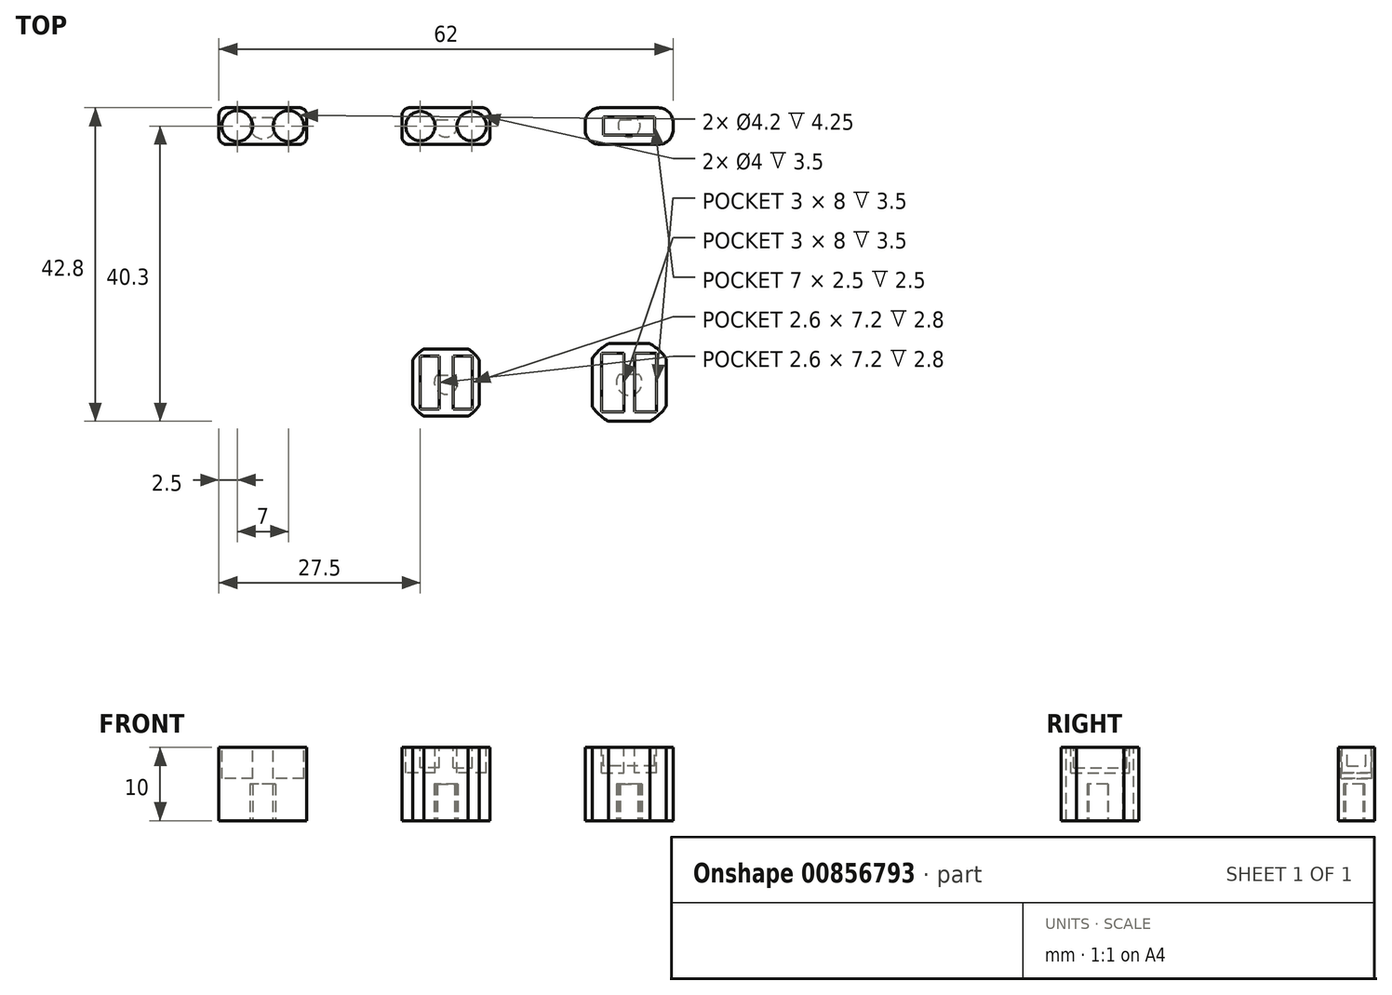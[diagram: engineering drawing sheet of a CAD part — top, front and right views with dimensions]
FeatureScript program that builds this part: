
annotation { "Feature Type Name" : "Feature", "Feature Type Description" : "" }
export const myFeature = defineFeature(function(context is Context, id is Id, definition is map)
    precondition{}
    {
        {
            var Q0;
            Q0=qCreatedBy(makeId("Top.planeOp"),FACE);
            var sketch = newSketch(context, id + "F0", { "sketchPlane" : qUnion([Q0])});
            skCircle(sketch, "E0", {"center": v(0, -10) * mm, "radius": 7 * mm});
            skLineSegment(sketch, "E1.bottom", {"start": v(6, -12.5) * mm, "end": v(-6, -12.5) * mm});
            skLineSegment(sketch, "E1.top", {"start": v(6, -7.5) * mm, "end": v(-6, -7.5) * mm});
            skLineSegment(sketch, "E1.left", {"start": v(6, -12.5) * mm, "end": v(6, -7.5) * mm});
            skLineSegment(sketch, "E1.right", {"start": v(-6, -12.5) * mm, "end": v(-6, -7.5) * mm});
            skCircle(sketch, "E2", {"center": v(-3.5, -10) * mm, "radius": 2 * mm});
            skCircle(sketch, "E3", {"center": v(3.5, -10) * mm, "radius": 2 * mm});
            skLineSegment(sketch, "E4", {"start": v(12.5, 0) * mm, "end": v(12.5, -20) * mm, "construction": true});
            skLineSegment(sketch, "E5.MirrorCS", {"start": v(31, -12.5) * mm, "end": v(31, -7.5) * mm});
            skLineSegment(sketch, "E6.MirrorCS", {"start": v(19, -7.5) * mm, "end": v(31, -7.5) * mm});
            skLineSegment(sketch, "E7.MirrorCS", {"start": v(19, -12.5) * mm, "end": v(31, -12.5) * mm});
            skLineSegment(sketch, "E8.MirrorCS", {"start": v(19, -12.5) * mm, "end": v(19, -7.5) * mm});
            skCircle(sketch, "E9.MirrorC", {"center": v(25, -10) * mm, "radius": 7 * mm});
            skLineSegment(sketch, "E10.bottom", {"start": v(28.5, -11.25) * mm, "end": v(21.5, -11.25) * mm});
            skLineSegment(sketch, "E10.top", {"start": v(28.5, -8.75) * mm, "end": v(21.5, -8.75) * mm});
            skLineSegment(sketch, "E10.left", {"start": v(28.5, -11.25) * mm, "end": v(28.5, -8.75) * mm});
            skLineSegment(sketch, "E10.right", {"start": v(21.5, -11.25) * mm, "end": v(21.5, -8.75) * mm});
            skCircle(sketch, "E11", {"center": v(0, -45) * mm, "radius": 7 * mm});
            skLineSegment(sketch, "E12.bottom", {"start": v(-0.95, -48.6) * mm, "end": v(-3.55, -48.6) * mm});
            skLineSegment(sketch, "E12.top", {"start": v(-0.95, -41.4) * mm, "end": v(-3.55, -41.4) * mm});
            skLineSegment(sketch, "E12.left", {"start": v(-0.95, -48.6) * mm, "end": v(-0.95, -41.4) * mm});
            skLineSegment(sketch, "E12.right", {"start": v(-3.55, -48.6) * mm, "end": v(-3.55, -41.4) * mm});
            skPoint(sketch, "E12.middle", {"position": v(-2.25, -45) * mm});
            skLineSegment(sketch, "E13", {"start": v(0, -45) * mm, "end": v(9.52, -45) * mm, "construction": true});
            skLineSegment(sketch, "E14.MirrorCS", {"start": v(0.95, -48.6) * mm, "end": v(0.95, -41.4) * mm});
            skLineSegment(sketch, "E15.MirrorCS", {"start": v(0.95, -41.4) * mm, "end": v(3.55, -41.4) * mm});
            skLineSegment(sketch, "E16.MirrorCS", {"start": v(0.95, -48.6) * mm, "end": v(3.55, -48.6) * mm});
            skLineSegment(sketch, "E17.MirrorCS", {"start": v(3.55, -48.6) * mm, "end": v(3.55, -41.4) * mm});
            skPoint(sketch, "E18.MirrorP", {"position": v(2.25, -45) * mm});
            skCircle(sketch, "E19", {"center": v(0, -45) * mm, "radius": 5.5 * mm});
            skLineSegment(sketch, "E20", {"start": v(-3.01, -40.4) * mm, "end": v(3.01, -40.4) * mm});
            skLineSegment(sketch, "E21", {"start": v(-4.55, -41.91) * mm, "end": v(-4.55, -48.09) * mm});
            skLineSegment(sketch, "E22.MirrorCS", {"start": v(4.55, -41.91) * mm, "end": v(4.55, -48.09) * mm});
            skLineSegment(sketch, "E23.MirrorCS", {"start": v(-3.01, -49.6) * mm, "end": v(3.01, -49.6) * mm});
            skCircle(sketch, "E24", {"center": v(25, -45) * mm, "radius": 6 * mm});
            skCircle(sketch, "E25", {"center": v(25, -45) * mm, "radius": 7 * mm});
            skLineSegment(sketch, "E26.bottom", {"start": v(28.75, -49) * mm, "end": v(25.75, -49) * mm});
            skLineSegment(sketch, "E26.top", {"start": v(28.75, -41) * mm, "end": v(25.75, -41) * mm});
            skLineSegment(sketch, "E26.left", {"start": v(28.75, -49) * mm, "end": v(28.75, -41) * mm});
            skLineSegment(sketch, "E26.right", {"start": v(25.75, -49) * mm, "end": v(25.75, -41) * mm});
            skPoint(sketch, "E26.middle", {"position": v(27.25, -45) * mm});
            skLineSegment(sketch, "E27", {"start": v(25, -45) * mm, "end": v(25, -28.58) * mm, "construction": true});
            skLineSegment(sketch, "E28.MirrorCS", {"start": v(21.25, -41) * mm, "end": v(24.25, -41) * mm});
            skLineSegment(sketch, "E29.MirrorCS", {"start": v(21.25, -49) * mm, "end": v(21.25, -41) * mm});
            skLineSegment(sketch, "E30.MirrorCS", {"start": v(24.25, -49) * mm, "end": v(24.25, -41) * mm});
            skLineSegment(sketch, "E31.MirrorCS", {"start": v(21.25, -49) * mm, "end": v(24.25, -49) * mm});
            skLineSegment(sketch, "E32", {"start": v(27.81, -50.3) * mm, "end": v(22.19, -50.3) * mm});
            skLineSegment(sketch, "E33", {"start": v(19.95, -48.24) * mm, "end": v(19.95, -41.76) * mm});
            skLineSegment(sketch, "E34", {"start": v(22.19, -39.7) * mm, "end": v(27.81, -39.7) * mm});
            skLineSegment(sketch, "E35", {"start": v(30.05, -41.76) * mm, "end": v(30.05, -48.24) * mm});
            skLineSegment(sketch, "E36", {"start": v(-12.5, -20.28) * mm, "end": v(-12.5, 0) * mm, "construction": true});
            skCircle(sketch, "E37.MirrorC", {"center": v(-25, -10) * mm, "radius": 7 * mm});
            skLineSegment(sketch, "E38.MirrorCS", {"start": v(-31, -12.5) * mm, "end": v(-19, -12.5) * mm});
            skLineSegment(sketch, "E39.MirrorCS", {"start": v(-19, -12.5) * mm, "end": v(-19, -7.5) * mm});
            skLineSegment(sketch, "E40.MirrorCS", {"start": v(-31, -7.5) * mm, "end": v(-19, -7.5) * mm});
            skLineSegment(sketch, "E41.MirrorCS", {"start": v(-31, -12.5) * mm, "end": v(-31, -7.5) * mm});
            skCircle(sketch, "E42", {"center": v(-28.5, -10) * mm, "radius": 2.1 * mm});
            skCircle(sketch, "E43", {"center": v(-21.5, -10) * mm, "radius": 2.1 * mm});
            skSolve(sketch);
        }
        {
            var Q0;
            Q0=makeQuery(id+"F0.imprint","IMPRINT",FACE,{"disambiguationData":[TD([[makeQuery(id+"F0.imprint","IMPRINT",EDGE,{"derivedFrom":sQuery(id+"F0.wireOp",EDGE,"E1.bottom")}),-1.0]])]});
            var Q1;
            Q1=makeQuery(id+"F0.imprint","IMPRINT",FACE,{"disambiguationData":[TD([[makeQuery(id+"F0.imprint","IMPRINT",EDGE,{"derivedFrom":sQuery(id+"F0.wireOp",EDGE,"E2")}),1.0]])]});
            var Q2;
            Q2=makeQuery(id+"F0.imprint","IMPRINT",FACE,{"disambiguationData":[TD([[makeQuery(id+"F0.imprint","IMPRINT",EDGE,{"derivedFrom":sQuery(id+"F0.wireOp",EDGE,"E3")}),1.0]])]});
            extrude(context, id + "F1", {"entities" : qUnion([Q0, Q1, Q2]), "oppositeDirection" : true, "depth" : 10 * mm, "offsetDistance" : 25 * mm});
        }
        {
            var Q0;
            Q0=makeQuery(id+"F0.imprint","IMPRINT",FACE,{"disambiguationData":[TD([[makeQuery(id+"F0.imprint","IMPRINT",EDGE,{"derivedFrom":sQuery(id+"F0.wireOp",EDGE,"E2")}),1.0]])]});
            var Q1;
            Q1=makeQuery(id+"F0.imprint","IMPRINT",FACE,{"disambiguationData":[TD([[makeQuery(id+"F0.imprint","IMPRINT",EDGE,{"derivedFrom":sQuery(id+"F0.wireOp",EDGE,"E3")}),1.0]])]});
            extrude(context, id + "F2", {"entities" : qUnion([Q0, Q1]), "operationType" : NewBodyOperationType.REMOVE, "oppositeDirection" : true, "depth" : 3.5 * mm, "offsetDistance" : 25 * mm});
        }
        {
            var Q0;
            Q0=makeQuery(id+"F1.opExtrude","CAP_FACE",FACE,{"disambiguationData":[OSD([sQuery(id+"F0.wireOp",EDGE,"E1.bottom"),sQuery(id+"F0.wireOp",EDGE,"E1.top"),sQuery(id+"F0.wireOp",EDGE,"E1.left"),sQuery(id+"F0.wireOp",EDGE,"E1.right")])],"isStart":false});
            var sketch = newSketch(context, id + "F3", { "sketchPlane" : qUnion([Q0])});
            skCircle(sketch, "E44", {"center": v(0, 10) * mm, "radius": 1.5 * mm});
            skPoint(sketch, "E44.centerSnap0", {"position": v(6, 10) * mm});
            skCircle(sketch, "E45", {"center": v(0, 10) * mm, "radius": 2.5 * mm});
            skLineSegment(sketch, "E46", {"start": v(-1.2, 9.1) * mm, "end": v(1.2, 9.1) * mm});
            skSolve(sketch);
        }
        {
            var Q0;
            Q0=makeQuery(id+"F1.opExtrude","SWEPT_EDGE",EDGE,{"disambiguationData":[OSD([sQuery(id+"F0.wireOp",EDGE,"E1.bottom"),sQuery(id+"F0.wireOp",EDGE,"E1.left")])]});
            var Q1;
            Q1=makeQuery(id+"F1.opExtrude","SWEPT_EDGE",EDGE,{"disambiguationData":[OSD([sQuery(id+"F0.wireOp",EDGE,"E1.top"),sQuery(id+"F0.wireOp",EDGE,"E1.left")])]});
            var Q2;
            Q2=makeQuery(id+"F1.opExtrude","SWEPT_EDGE",EDGE,{"disambiguationData":[OSD([sQuery(id+"F0.wireOp",EDGE,"E1.bottom"),sQuery(id+"F0.wireOp",EDGE,"E1.right")])]});
            var Q3;
            Q3=makeQuery(id+"F1.opExtrude","SWEPT_EDGE",EDGE,{"disambiguationData":[OSD([sQuery(id+"F0.wireOp",EDGE,"E1.top"),sQuery(id+"F0.wireOp",EDGE,"E1.right")])]});
            fillet(context, id + "F4", {"entities" : qUnion([Q0, Q1, Q2, Q3]), "radius" : 1 * mm, "tangentPropagation" : true, "allowEdgeOverflow" : false});
        }
        {
            var Q0;
            Q0=makeQuery(id+"F0.imprint","IMPRINT",FACE,{"disambiguationData":[TD([[makeQuery(id+"F0.imprint","IMPRINT",EDGE,{"derivedFrom":sQuery(id+"F0.wireOp",EDGE,"E5.MirrorCS")}),1.0]])]});
            var Q1;
            Q1=makeQuery(id+"F0.imprint","IMPRINT",FACE,{"disambiguationData":[TD([[makeQuery(id+"F0.imprint","IMPRINT",EDGE,{"derivedFrom":sQuery(id+"F0.wireOp",EDGE,"E10.bottom")}),-1.0]])]});
            extrude(context, id + "F5", {"entities" : qUnion([Q0, Q1]), "oppositeDirection" : true, "depth" : 10 * mm, "offsetDistance" : 25 * mm});
        }
        {
            var Q0;
            Q0=makeQuery(id+"F5.opExtrude","CAP_FACE",FACE,{"disambiguationData":[OSD([sQuery(id+"F0.wireOp",EDGE,"E5.MirrorCS"),sQuery(id+"F0.wireOp",EDGE,"E6.MirrorCS"),sQuery(id+"F0.wireOp",EDGE,"E7.MirrorCS"),sQuery(id+"F0.wireOp",EDGE,"E8.MirrorCS")])],"isStart":false});
            var sketch = newSketch(context, id + "F6", { "sketchPlane" : qUnion([Q0])});
            skCircle(sketch, "E47", {"center": v(25, 10) * mm, "radius": 2.5 * mm});
            skPoint(sketch, "E47.centerSnap0", {"position": v(19, 10) * mm});
            skPoint(sketch, "E47.centerSnap1", {"position": v(25, 12.5) * mm});
            skCircle(sketch, "E48", {"center": v(25, 10) * mm, "radius": 1.5 * mm});
            skLineSegment(sketch, "E49", {"start": v(23.8, 9.1) * mm, "end": v(26.2, 9.1) * mm});
            skSolve(sketch);
        }
        {
            var Q0;
            Q0=makeQuery(id+"F0.imprint","IMPRINT",FACE,{"disambiguationData":[TD([[makeQuery(id+"F0.imprint","IMPRINT",EDGE,{"derivedFrom":sQuery(id+"F0.wireOp",EDGE,"E10.bottom")}),-1.0]])]});
            extrude(context, id + "F7", {"entities" : qUnion([Q0]), "operationType" : NewBodyOperationType.REMOVE, "oppositeDirection" : true, "depth" : 2.5 * mm, "offsetDistance" : 25 * mm});
        }
        {
            var Q0;
            {var subQ0=sQuery(id+"F6.wireOp",EDGE,"E49");Q0=makeQuery(id+"F6.imprint","IMPRINT",FACE,{"disambiguationData":[TD([[makeQuery(id+"F6.imprint","IMPRINT",EDGE,{"derivedFrom":subQ0}),1.0]])]});}
            extrude(context, id + "F8", {"entities" : qUnion([Q0]), "operationType" : NewBodyOperationType.REMOVE, "oppositeDirection" : true, "depth" : 5 * mm, "offsetDistance" : 25 * mm});
        }
        {
            var Q0;
            Q0=makeQuery(id+"F5.opExtrude","SWEPT_EDGE",EDGE,{"disambiguationData":[OSD([sQuery(id+"F0.wireOp",EDGE,"E7.MirrorCS"),sQuery(id+"F0.wireOp",EDGE,"E8.MirrorCS")])]});
            var Q1;
            Q1=makeQuery(id+"F5.opExtrude","SWEPT_EDGE",EDGE,{"disambiguationData":[OSD([sQuery(id+"F0.wireOp",EDGE,"E5.MirrorCS"),sQuery(id+"F0.wireOp",EDGE,"E7.MirrorCS")])]});
            var Q2;
            Q2=makeQuery(id+"F5.opExtrude","SWEPT_EDGE",EDGE,{"disambiguationData":[OSD([sQuery(id+"F0.wireOp",EDGE,"E5.MirrorCS"),sQuery(id+"F0.wireOp",EDGE,"E6.MirrorCS")])]});
            var Q3;
            Q3=makeQuery(id+"F5.opExtrude","SWEPT_EDGE",EDGE,{"disambiguationData":[OSD([sQuery(id+"F0.wireOp",EDGE,"E6.MirrorCS"),sQuery(id+"F0.wireOp",EDGE,"E8.MirrorCS")])]});
            fillet(context, id + "F9", {"entities" : qUnion([Q0, Q1, Q2, Q3]), "radius" : 2 * mm, "tangentPropagation" : true, "allowEdgeOverflow" : false});
        }
        {
            var Q0;
            {var subQ0=sQuery(id+"F3.wireOp",EDGE,"E46");Q0=makeQuery(id+"F3.imprint","IMPRINT",FACE,{"disambiguationData":[TD([[makeQuery(id+"F3.imprint","IMPRINT",EDGE,{"derivedFrom":subQ0}),1.0]])]});}
            extrude(context, id + "F10", {"entities" : qUnion([Q0]), "operationType" : NewBodyOperationType.REMOVE, "oppositeDirection" : true, "depth" : 5 * mm, "offsetDistance" : 25 * mm});
        }
        {
            var Q0;
            Q0=makeQuery(id+"F0.imprint","IMPRINT",FACE,{"disambiguationData":[TD([[makeQuery(id+"F0.imprint","IMPRINT",EDGE,{"derivedFrom":sQuery(id+"F0.wireOp",EDGE,"E12.bottom")}),1.0]])]});
            var Q1;
            Q1=makeQuery(id+"F0.imprint","IMPRINT",FACE,{"disambiguationData":[TD([[makeQuery(id+"F0.imprint","IMPRINT",EDGE,{"derivedFrom":sQuery(id+"F0.wireOp",EDGE,"E12.bottom")}),-1.0]])]});
            var Q2;
            Q2=makeQuery(id+"F0.imprint","IMPRINT",FACE,{"disambiguationData":[TD([[makeQuery(id+"F0.imprint","IMPRINT",EDGE,{"derivedFrom":sQuery(id+"F0.wireOp",EDGE,"E14.MirrorCS")}),-1.0]])]});
            extrude(context, id + "F11", {"entities" : qUnion([Q0, Q1, Q2]), "oppositeDirection" : true, "depth" : 10 * mm, "offsetDistance" : 25 * mm});
        }
        {
            var Q0;
            Q0=makeQuery(id+"F0.imprint","IMPRINT",FACE,{"disambiguationData":[TD([[makeQuery(id+"F0.imprint","IMPRINT",EDGE,{"derivedFrom":sQuery(id+"F0.wireOp",EDGE,"E12.bottom")}),-1.0]])]});
            var Q1;
            Q1=makeQuery(id+"F0.imprint","IMPRINT",FACE,{"disambiguationData":[TD([[makeQuery(id+"F0.imprint","IMPRINT",EDGE,{"derivedFrom":sQuery(id+"F0.wireOp",EDGE,"E14.MirrorCS")}),-1.0]])]});
            extrude(context, id + "F12", {"entities" : qUnion([Q0, Q1]), "operationType" : NewBodyOperationType.REMOVE, "oppositeDirection" : true, "depth" : 2.8 * mm, "offsetDistance" : 25 * mm});
        }
        {
            var Q0;
            Q0=makeQuery(id+"F11.opExtrude","CAP_FACE",FACE,{"disambiguationData":[OSD([sQuery(id+"F0.wireOp",EDGE,"E19")])],"isStart":false});
            var sketch = newSketch(context, id + "F13", { "sketchPlane" : qUnion([Q0])});
            skCircle(sketch, "E50", {"center": v(0, 45) * mm, "radius": 1.6 * mm});
            skLineSegment(sketch, "E51", {"start": v(-1.25, 44) * mm, "end": v(1.25, 44) * mm});
            skSolve(sketch);
        }
        {
            var Q0;
            {var subQ0=sQuery(id+"F13.wireOp",EDGE,"E51");Q0=makeQuery(id+"F13.imprint","IMPRINT",FACE,{"disambiguationData":[TD([[makeQuery(id+"F13.imprint","IMPRINT",EDGE,{"derivedFrom":subQ0}),1.0]])]});}
            extrude(context, id + "F14", {"entities" : qUnion([Q0]), "operationType" : NewBodyOperationType.REMOVE, "oppositeDirection" : true, "depth" : 5 * mm, "offsetDistance" : 25 * mm});
        }
        {
            var Q0;
            Q0=makeQuery(id+"F0.imprint","IMPRINT",FACE,{"disambiguationData":[TD([[makeQuery(id+"F0.imprint","IMPRINT",EDGE,{"derivedFrom":sQuery(id+"F0.wireOp",EDGE,"E24")}),1.0]])]});
            var Q1;
            Q1=makeQuery(id+"F0.imprint","IMPRINT",FACE,{"disambiguationData":[TD([[makeQuery(id+"F0.imprint","IMPRINT",EDGE,{"derivedFrom":sQuery(id+"F0.wireOp",EDGE,"E28.MirrorCS")}),-1.0]])]});
            var Q2;
            Q2=makeQuery(id+"F0.imprint","IMPRINT",FACE,{"disambiguationData":[TD([[makeQuery(id+"F0.imprint","IMPRINT",EDGE,{"derivedFrom":sQuery(id+"F0.wireOp",EDGE,"E26.bottom")}),-1.0]])]});
            extrude(context, id + "F15", {"entities" : qUnion([Q0, Q1, Q2]), "oppositeDirection" : true, "depth" : 10 * mm, "offsetDistance" : 25 * mm});
        }
        {
            var Q0;
            Q0=makeQuery(id+"F0.imprint","IMPRINT",FACE,{"disambiguationData":[TD([[makeQuery(id+"F0.imprint","IMPRINT",EDGE,{"derivedFrom":sQuery(id+"F0.wireOp",EDGE,"E28.MirrorCS")}),-1.0]])]});
            var Q1;
            Q1=makeQuery(id+"F0.imprint","IMPRINT",FACE,{"disambiguationData":[TD([[makeQuery(id+"F0.imprint","IMPRINT",EDGE,{"derivedFrom":sQuery(id+"F0.wireOp",EDGE,"E26.bottom")}),-1.0]])]});
            extrude(context, id + "F16", {"entities" : qUnion([Q0, Q1]), "operationType" : NewBodyOperationType.REMOVE, "surfaceOperationType" : NewSurfaceOperationType.ADD, "oppositeDirection" : true, "depth" : 3.5 * mm, "offsetDistance" : 25 * mm});
        }
        {
            var Q0;
            Q0=makeQuery(id+"F15.opExtrude","CAP_FACE",FACE,{"disambiguationData":[OSD([sQuery(id+"F0.wireOp",EDGE,"E24")])],"isStart":false});
            var sketch = newSketch(context, id + "F17", { "sketchPlane" : qUnion([Q0])});
            skCircle(sketch, "E52", {"center": v(25, 45) * mm, "radius": 1.75 * mm});
            skLineSegment(sketch, "E53", {"start": v(26.36, 43.9) * mm, "end": v(23.64, 43.9) * mm});
            skSolve(sketch);
        }
        {
            var Q0;
            {var subQ0=sQuery(id+"F17.wireOp",EDGE,"E53");Q0=makeQuery(id+"F17.imprint","IMPRINT",FACE,{"disambiguationData":[TD([[makeQuery(id+"F17.imprint","IMPRINT",EDGE,{"derivedFrom":subQ0}),-1.0]])]});}
            extrude(context, id + "F18", {"entities" : qUnion([Q0]), "operationType" : NewBodyOperationType.REMOVE, "oppositeDirection" : true, "depth" : 5 * mm, "offsetDistance" : 25 * mm});
        }
        {
            var Q0;
            Q0=makeQuery(id+"F0.imprint","IMPRINT",FACE,{"disambiguationData":[TD([[makeQuery(id+"F0.imprint","IMPRINT",EDGE,{"derivedFrom":sQuery(id+"F0.wireOp",EDGE,"E38.MirrorCS")}),1.0]])]});
            var Q1;
            Q1=makeQuery(id+"F0.imprint","IMPRINT",FACE,{"disambiguationData":[TD([[makeQuery(id+"F0.imprint","IMPRINT",EDGE,{"derivedFrom":sQuery(id+"F0.wireOp",EDGE,"E43")}),1.0]])]});
            var Q2;
            Q2=makeQuery(id+"F0.imprint","IMPRINT",FACE,{"disambiguationData":[TD([[makeQuery(id+"F0.imprint","IMPRINT",EDGE,{"derivedFrom":sQuery(id+"F0.wireOp",EDGE,"E42")}),1.0]])]});
            extrude(context, id + "F19", {"entities" : qUnion([Q0, Q1, Q2]), "oppositeDirection" : true, "depth" : 10 * mm, "offsetDistance" : 25 * mm});
        }
        {
            var Q0;
            Q0=makeQuery(id+"F0.imprint","IMPRINT",FACE,{"disambiguationData":[TD([[makeQuery(id+"F0.imprint","IMPRINT",EDGE,{"derivedFrom":sQuery(id+"F0.wireOp",EDGE,"E43")}),1.0]])]});
            var Q1;
            Q1=makeQuery(id+"F0.imprint","IMPRINT",FACE,{"disambiguationData":[TD([[makeQuery(id+"F0.imprint","IMPRINT",EDGE,{"derivedFrom":sQuery(id+"F0.wireOp",EDGE,"E42")}),1.0]])]});
            extrude(context, id + "F20", {"entities" : qUnion([Q0, Q1]), "operationType" : NewBodyOperationType.REMOVE, "oppositeDirection" : true, "depth" : 4.25 * mm, "offsetDistance" : 25 * mm});
        }
        {
            var Q0;
            Q0=makeQuery(id+"F19.opExtrude","CAP_FACE",FACE,{"disambiguationData":[OSD([sQuery(id+"F0.wireOp",EDGE,"E38.MirrorCS"),sQuery(id+"F0.wireOp",EDGE,"E39.MirrorCS"),sQuery(id+"F0.wireOp",EDGE,"E40.MirrorCS"),sQuery(id+"F0.wireOp",EDGE,"E41.MirrorCS")])],"isStart":false});
            var sketch = newSketch(context, id + "F21", { "sketchPlane" : qUnion([Q0])});
            skCircle(sketch, "E54", {"center": v(-25, 10) * mm, "radius": 1.75 * mm});
            skPoint(sketch, "E54.centerSnap0", {"position": v(-19, 10) * mm});
            skPoint(sketch, "E54.centerSnap1", {"position": v(-25, 7.5) * mm});
            skLineSegment(sketch, "E55", {"start": v(-23.64, 8.9) * mm, "end": v(-26.36, 8.9) * mm});
            skSolve(sketch);
        }
        {
            var Q0;
            {var subQ0=sQuery(id+"F21.wireOp",EDGE,"E55");Q0=makeQuery(id+"F21.imprint","IMPRINT",FACE,{"disambiguationData":[TD([[makeQuery(id+"F21.imprint","IMPRINT",EDGE,{"derivedFrom":subQ0}),-1.0]])]});}
            extrude(context, id + "F22", {"entities" : qUnion([Q0]), "operationType" : NewBodyOperationType.REMOVE, "oppositeDirection" : true, "depth" : 5 * mm, "offsetDistance" : 25 * mm});
        }
        {
            var Q0;
            Q0=makeQuery(id+"F19.opExtrude","SWEPT_EDGE",EDGE,{"disambiguationData":[OSD([sQuery(id+"F0.wireOp",EDGE,"E40.MirrorCS"),sQuery(id+"F0.wireOp",EDGE,"E41.MirrorCS")])]});
            var Q1;
            Q1=makeQuery(id+"F19.opExtrude","SWEPT_EDGE",EDGE,{"disambiguationData":[OSD([sQuery(id+"F0.wireOp",EDGE,"E38.MirrorCS"),sQuery(id+"F0.wireOp",EDGE,"E41.MirrorCS")])]});
            var Q2;
            Q2=makeQuery(id+"F19.opExtrude","SWEPT_EDGE",EDGE,{"disambiguationData":[OSD([sQuery(id+"F0.wireOp",EDGE,"E39.MirrorCS"),sQuery(id+"F0.wireOp",EDGE,"E40.MirrorCS")])]});
            var Q3;
            Q3=makeQuery(id+"F19.opExtrude","SWEPT_EDGE",EDGE,{"disambiguationData":[OSD([sQuery(id+"F0.wireOp",EDGE,"E38.MirrorCS"),sQuery(id+"F0.wireOp",EDGE,"E39.MirrorCS")])]});
            fillet(context, id + "F23", {"entities" : qUnion([Q0, Q1, Q2, Q3]), "radius" : 1 * mm, "tangentPropagation" : true, "allowEdgeOverflow" : false});
        }
    });
